# Revit family: Electrical_Switchgear_Modelec_Fascination-Collection-double-vertical_FRA88
name_source: partatom
category: Installations électriques
units: mm (PartAtom-declared; Revit-internal decimal feet)

## family parameters
Conserver l'orientation des annotations = Non
Cote de connecteur circulaire = Utiliser le diamètre
Couper avec des vides une fois chargée = Non
Hôte = Face
Numéro OmniClass = 23.80.50.11.14
Partagée = Non
Repere pour localisation dans la piece = Non
Titre OmniClass = Switches
Type d'élément = Normal

## types (1)
- Par défaut - veuillez charger le catalogue des types de familles Revit
    Apparent Load = 0 VA
    B1 = Oui
    B1 Bas = Oui
    B1 Haut = Oui
    B2 = Non
    B2 Bas = Non
    B2 Haut = Non
    C3 Bas = Non
    Couleur du Mécanisme Bas = Modelec - Metallique - Noir
    Couleur du Mécanisme Centre = Modelec - Metallique - Noir
    Couleur du Mécanisme Haut = Modelec - Metallique - Noir
    Description du Connecteur Bas = Interrupteur
    Description du Connecteur Centre = Interrupteur
    Description du Connecteur Haut = Interrupteur
    Elévation par défaut = 0 mm  [stored 0 ft]
    Fabricant = Modelec
    K1 Bas = Non
    K1 Haut = Non
    M1 Bas = Non
    M2 Bas = Non
    Modèle = Fascination collection
    Number of Poles = 1
    P1 = Non
    P1 Bas = Non
    P1 Haut = Non
    P2 = Non
    P2 Bas = Non
    P2 Haut = Non
    Power Factor = 1
    Quantité 1 = 3
    Quantité 2 = 3
    Quantité 3 = 3
    Quantité 4 = 3
    Quantité 5 = 3
    R1 Bas = Non
    R1 Haut = Non
    URL = https://www.modelec.com
    Version = 1
    Voltage = 220 V
    Weight - Mass = 0.20 kg
    zBoîteVisible = Oui
    zBoîteVisibleCentre = Non
    zZonedeMasquageCentreVisibleB = Oui
    zZonedeMasquageCentreVisibleP = Non
    zZonedeMasquageVisibleàDroiteetàGaucheB = Non
    zZonedeMasquageVisibleàDroiteetàGaucheP = Non
    М1 Haut = Non
    М2 Haut = Non

note: [stored X ft] marks values corroborated as IEEE doubles in the binary element streams (Revit-internal decimal feet)

## geometry (parser evidence)
native form markers: Sweep x1
no freeform markers — native parametric forms only
